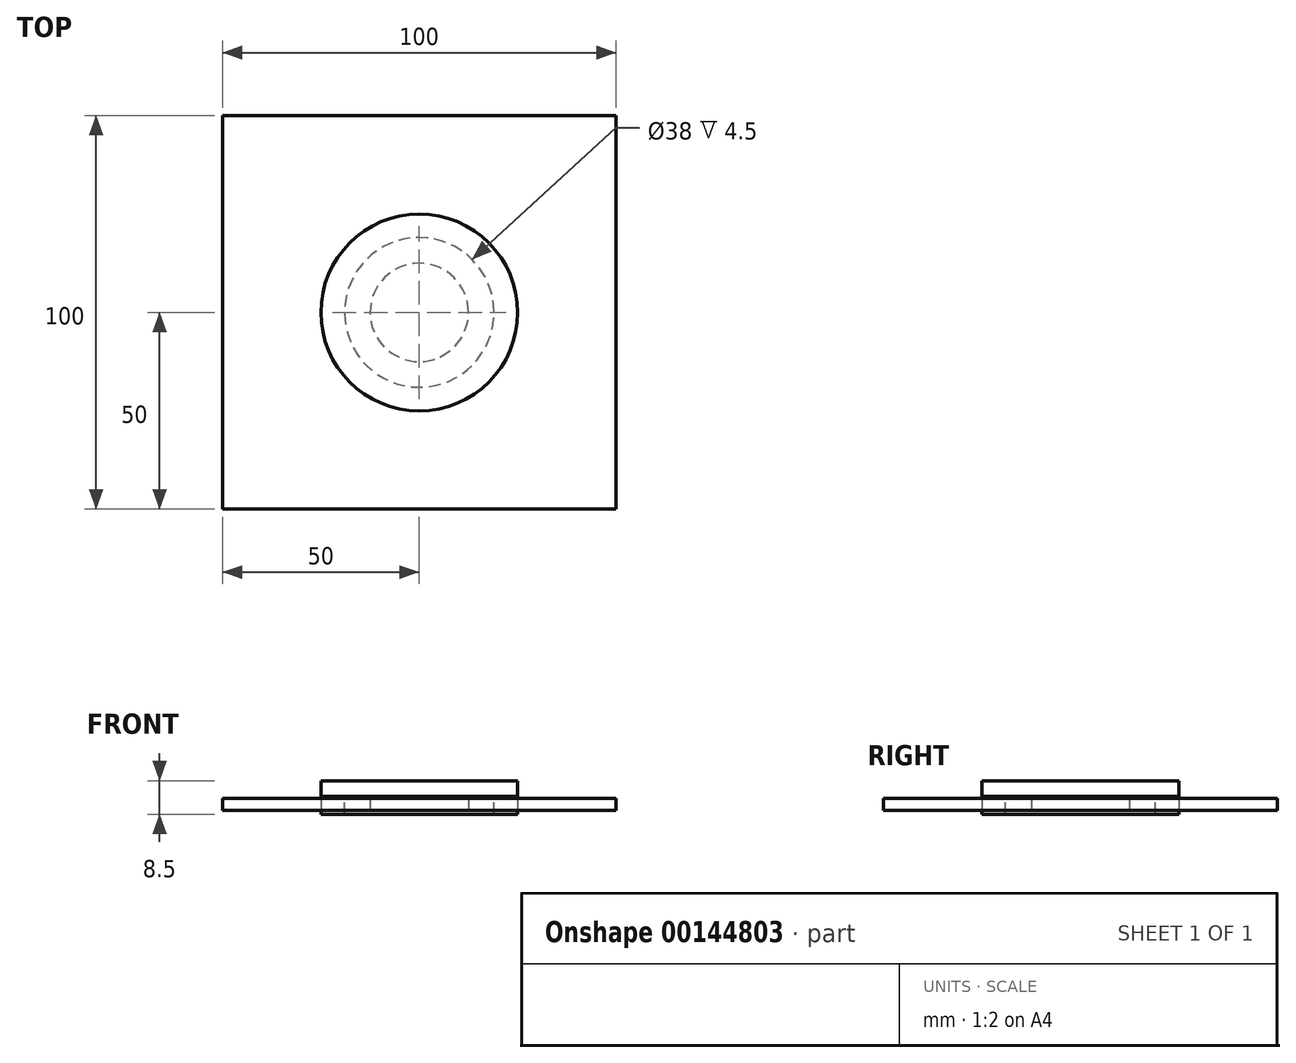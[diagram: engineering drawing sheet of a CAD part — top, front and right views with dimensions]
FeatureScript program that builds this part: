
annotation { "Feature Type Name" : "Feature", "Feature Type Description" : "" }
export const myFeature = defineFeature(function(context is Context, id is Id, definition is map)
    precondition{}
    {
        {
            var Q0;
            Q0=qCreatedBy(makeId("Top.planeOp"),FACE);
            var sketch = newSketch(context, id + "F0", { "sketchPlane" : qUnion([Q0])});
            skCircle(sketch, "E0", {"center": v(0, 0) * mm, "radius": 25 * mm});
            skSolve(sketch);
        }
        {
            var Q0;
            Q0 = qSketchRegion(id + "F0", true);
            extrude(context, id + "F1", {"entities" : qUnion([Q0]), "depth" : 4.5 * mm});
        }
        {
            var Q0;
            Q0=makeQuery(id+"F1.opExtrude","CAP_FACE",FACE,{"disambiguationData":[OSD([sQuery(id+"F0.wireOp",EDGE,"E0")])],"isStart":false});
            var sketch = newSketch(context, id + "F2", { "sketchPlane" : qUnion([Q0])});
            skCircle(sketch, "E1", {"center": v(0, 0) * mm, "radius": 19 * mm});
            skSolve(sketch);
        }
        {
            var Q0;
            Q0 = qSketchRegion(id + "F2", true);
            extrude(context, id + "F3", {"entities" : qUnion([Q0]), "operationType" : NewBodyOperationType.REMOVE, "oppositeDirection" : true, "depth" : 4.5 * mm});
        }
        {
            var Q0;
            Q0=qCreatedBy(makeId("Top.planeOp"),FACE);
            var sketch = newSketch(context, id + "F4", { "sketchPlane" : qUnion([Q0])});
            skCircle(sketch, "E2", {"center": v(0, 0) * mm, "radius": 12.5 * mm});
            skSolve(sketch);
        }
        {
            var Q0;
            Q0 = qSketchRegion(id + "F4", true);
            extrude(context, id + "F5", {"entities" : qUnion([Q0]), "depth" : 4.5 * mm});
        }
        {
            var Q0;
            Q0=qCreatedBy(makeId("Top.planeOp"),FACE);
            var sketch = newSketch(context, id + "F6", { "sketchPlane" : qUnion([Q0])});
            skLineSegment(sketch, "E3.bottom", {"start": v(-50, 50) * mm, "end": v(50, 50) * mm});
            skLineSegment(sketch, "E3.top", {"start": v(-50, -50) * mm, "end": v(50, -50) * mm});
            skLineSegment(sketch, "E3.left", {"start": v(-50, 50) * mm, "end": v(-50, -50) * mm});
            skLineSegment(sketch, "E3.right", {"start": v(50, 50) * mm, "end": v(50, -50) * mm});
            skSolve(sketch);
        }
        {
            var Q0;
            Q0 = qSketchRegion(id + "F6", true);
            extrude(context, id + "F7", {"entities" : qUnion([Q0]), "depth" : 4 * mm, "hasSecondDirection" : true, "secondDirectionOppositeDirection" : false, "secondDirectionDepth" : 1 * mm});
        }
        {
            var Q0;
            Q0=qCreatedBy(makeId("Top.planeOp"),FACE);
            var sketch = newSketch(context, id + "F8", { "sketchPlane" : qUnion([Q0])});
            skCircle(sketch, "E4", {"center": v(0, 0) * mm, "radius": 25 * mm});
            skSolve(sketch);
        }
        {
            var Q0;
            Q0 = qSketchRegion(id + "F8", true);
            extrude(context, id + "F9", {"entities" : qUnion([Q0]), "depth" : 8.5 * mm, "hasSecondDirection" : true, "secondDirectionOppositeDirection" : false, "secondDirectionDepth" : 4 * mm});
        }
    });
